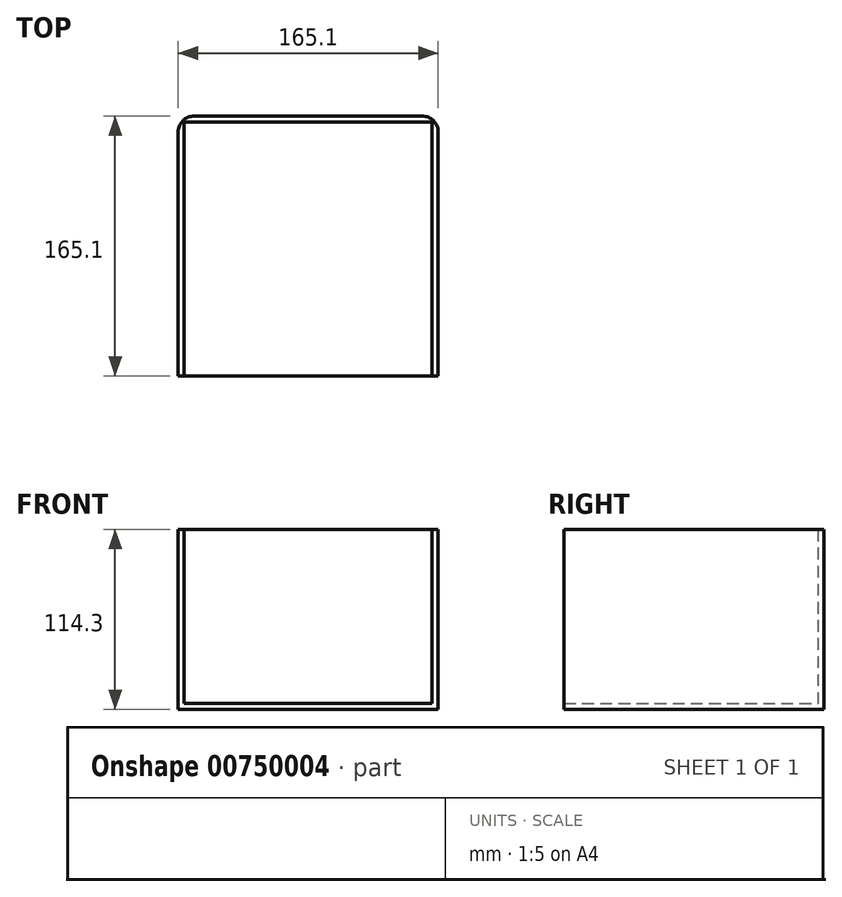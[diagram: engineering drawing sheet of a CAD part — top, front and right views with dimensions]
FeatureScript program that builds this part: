
annotation { "Feature Type Name" : "Feature", "Feature Type Description" : "" }
export const myFeature = defineFeature(function(context is Context, id is Id, definition is map)
    precondition{}
    {
        {
            var Q0;
            Q0=qCreatedBy(makeId("Front.planeOp"),FACE);
            var sketch = newSketch(context, id + "F0", { "sketchPlane" : qUnion([Q0])});
            skLineSegment(sketch, "E0.bottom", {"start": v(82.55, 57.15) * mm, "end": v(-82.55, 57.15) * mm});
            skLineSegment(sketch, "E0.top", {"start": v(82.55, -57.15) * mm, "end": v(-82.55, -57.15) * mm});
            skLineSegment(sketch, "E0.left", {"start": v(82.55, 57.15) * mm, "end": v(82.55, -57.15) * mm});
            skLineSegment(sketch, "E0.right", {"start": v(-82.55, 57.15) * mm, "end": v(-82.55, -57.15) * mm});
            skPoint(sketch, "E0.middle", {"position": v(0, 0) * mm});
            skSolve(sketch);
        }
        {
            var Q0;
            Q0 = qSketchRegion(id + "F0", true);
            extrude(context, id + "F1", {"entities" : qUnion([Q0]), "depth" : 165.1 * mm, "offsetDistance" : 25.4 * mm});
        }
        {
            var Q0;
            Q0=makeQuery(id+"F1.opExtrude","CAP_FACE",FACE,{"disambiguationData":[OSD([sQuery(id+"F0.wireOp",EDGE,"E0.bottom"),sQuery(id+"F0.wireOp",EDGE,"E0.top"),sQuery(id+"F0.wireOp",EDGE,"E0.left"),sQuery(id+"F0.wireOp",EDGE,"E0.right")])],"isStart":false});
            var Q1;
            Q1=makeQuery(id+"F1.opExtrude","SWEPT_FACE",FACE,{"disambiguationData":[OSD([sQuery(id+"F0.wireOp",EDGE,"E0.bottom")])]});
            shell(context, id + "F2", {"entities" : qUnion([Q0, Q1]), "thickness" : 3.8 * mm});
        }
        {
            var Q0;
            Q0=makeQuery(id+"F1.opExtrude","CAP_EDGE",EDGE,{"disambiguationData":[OSD([sQuery(id+"F0.wireOp",EDGE,"E0.left")])],"isStart":true});
            var Q1;
            Q1=makeQuery(id+"F1.opExtrude","CAP_EDGE",EDGE,{"disambiguationData":[OSD([sQuery(id+"F0.wireOp",EDGE,"E0.right")])],"isStart":true});
            fillet(context, id + "F3", {"entities" : qUnion([Q0, Q1]), "radius" : 10.16 * mm, "tangentPropagation" : true, "allowEdgeOverflow" : false});
        }
    });
